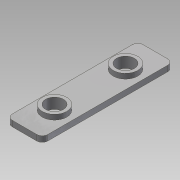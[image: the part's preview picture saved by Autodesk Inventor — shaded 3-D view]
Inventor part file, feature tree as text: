
AUTODESK INVENTOR PART (.ipt)
format: ipt  version: 2013 SP2 (Build 170200200, 200)  size: 107,008 bytes
history: native  units: mm
features: sketch x3, extrude x2, hole x1, fillet x1, projected_geometry x1
ambient origin geometry x8: Origin, YZ Plane, XZ Plane, XY Plane, X Axis, Y Axis, Z Axis, Center Point
bodies: Solid1 (feature_tree)
feature tree (8):
  extrude  "Extrusion1"  Depth=36.88mm
  extrude  "Extrusion2"  Depth=6.9mm
  hole  "Hole1"  [1 undecoded]
  fillet  "Fillet1"  Radius=1.4mm
  sketch  "Sketch1"  dims[d0=10.0mm d1=36.88mm]
  sketch  "Sketch2"  dims[d2=1.6mm d3=0.0mm d5=6.9mm]
  sketch  "Sketch3"  dims[d7=8.44mm d8=5.0mm d9=1.4mm d10=0.0mm d11=5.0mm d12=6.0mm d13=4.0mm d14=2.0mm d15=90.0deg d16=8.0mm d17=20.594885mm d18=1.51mm]
  projected_geometry  "Projected Loop1"
note: 1 required parameter value undecoded (feature->parameter linkage not recoverable at this tier; creation-order binding heuristic only, values carry confidence <= 0.55)
